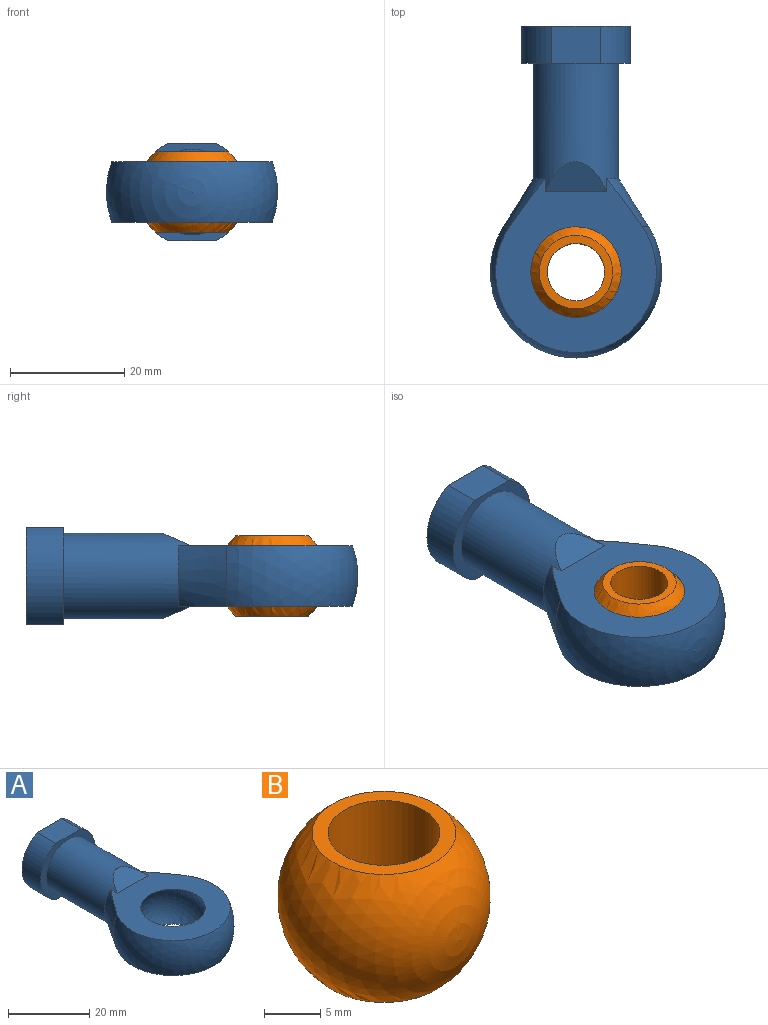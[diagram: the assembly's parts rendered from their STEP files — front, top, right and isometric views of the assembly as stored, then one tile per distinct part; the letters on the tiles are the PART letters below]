
ASSEMBLY  parts=2 mates=1
PART A: 20 faces, bbox 30x58x30 mm
  f0: sphere r=15mm, area 675.1mm2, adj f1,f3,f4,f5
  f1: cone r=6.36mm half-angle=32deg, axis (0,-1,0), area 109.3mm2, adj f0,f4,f5,f6
  f2: sphere r=9.5mm, area 626.8mm2, adj f4,f5
  f3: cone r=6.36mm half-angle=32deg, axis (0,-1,0), area 109.3mm2, adj f0,f4,f5,f6
  f4: plane 31.05x28.1mm, normal (0,0,1), area 442.8mm2, adj f0,f1,f2,f3,f6,f17
  f5: plane 31.05x28.1mm, normal (0,0,-1), area 442.8mm2, adj f0,f1,f2,f3,f6,f16
  f6: cylinder r=7.5mm len=22.5mm, axis (0,-1,0), area 923.3mm2, adj f1,f3,f4,f5,f13,f16,f17
  f7: cylinder r=4mm len=8mm, axis (0,1,0), area 83.8mm2, adj f8,f11
  f8: cone r=2mm half-angle=60deg, axis (0,1,0), area 58mm2, adj f7
  f9: cone r=4.5mm half-angle=45deg, axis (0,1,0), area 40.2mm2, adj f10,f19
  f10: cylinder r=4mm len=19mm, axis (0,1,0), area 476.8mm2, adj f9,f11
  f11: plane 8x8mm, normal (0,-1,0), area 0.1mm2, adj f7,f10
  f12: plane 8.49x6.5mm, normal (0,0,-1), area 55.2mm2, adj f13,f14,f18,f19
  f13: plane 19x17mm, normal (0,-1,0), area 95.4mm2, adj f6,f12,f14,f15,f18
  f14: cylinder r=9.5mm len=17mm, axis (0,-1,0), area 136.8mm2, adj f12,f13,f15,f19
  f15: plane 8.49x6.5mm, normal (0,0,1), area 55.2mm2, adj f13,f14,f18,f19
  f16: plane 10.71x5.3mm, normal (0,-0.39,-0.92), area 42.5mm2, adj f5,f6
  f17: plane 10.71x5.3mm, normal (0,-0.39,0.92), area 42.5mm2, adj f4,f6
  f18: cylinder r=9.5mm len=17mm, axis (0,-1,0), area 136.8mm2, adj f12,f13,f15,f19
  f19: plane 19x17mm, normal (0,1,0), area 193.6mm2, adj f9,f12,f14,f15,f18
PART B: 4 faces, bbox 19x19x19 mm
  f0: sphere r=9.5mm, area 835.7mm2, adj f2,f3
  f1: cylinder r=5mm len=14mm, axis (0,0,1), area 439.8mm2, adj f2,f3
  f2: plane 12.85x12.85mm, normal (0,0,-1), area 51.1mm2, adj f0,f1
  f3: plane 12.85x12.85mm, normal (0,0,1), area 51.1mm2, adj f0,f1
PLACE A at identity
PLACE B rot(axis=(0,0,-1),13.1deg) t=(0,0,0)mm
MATE ball B.f1 <-> A.f2  axis (0,0,1) through (0,0,0)mm
